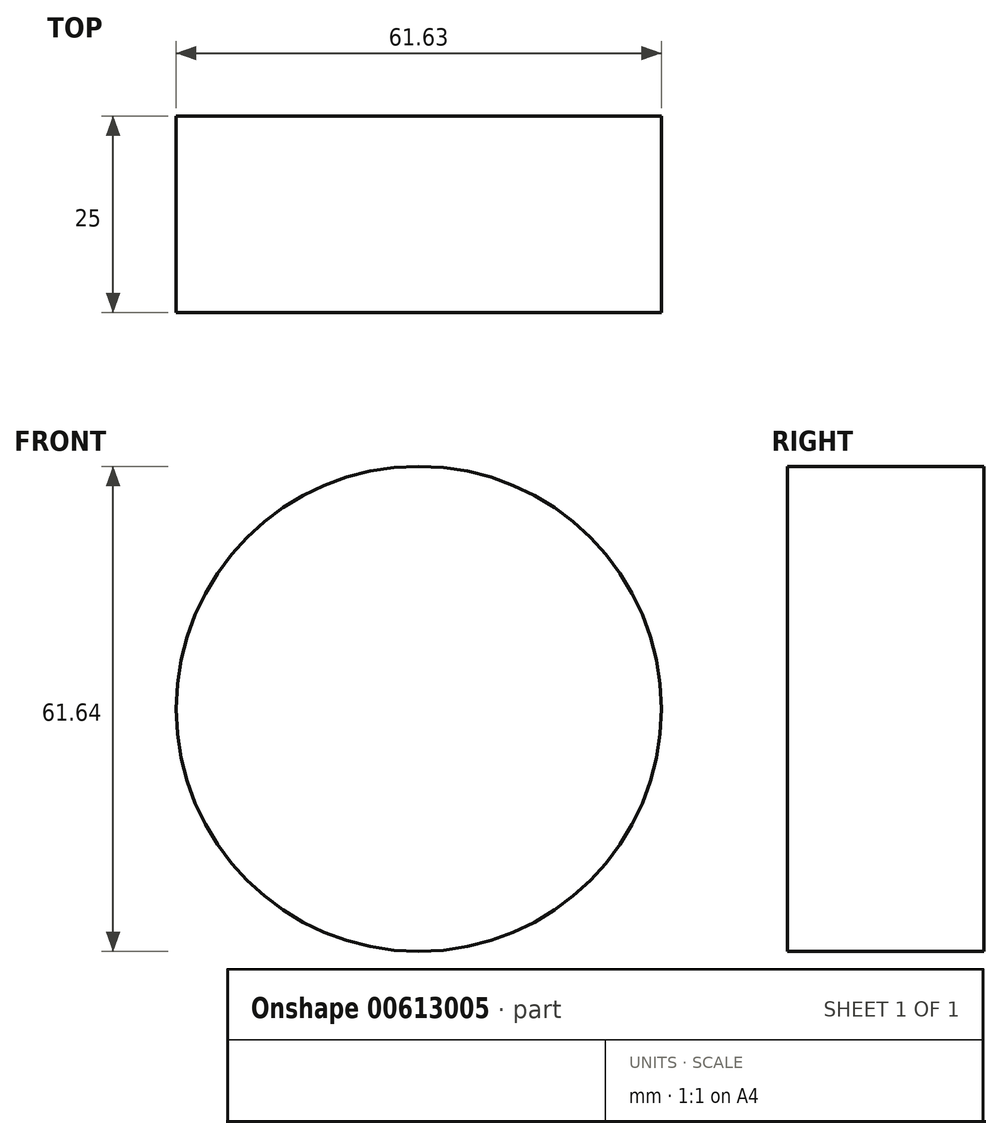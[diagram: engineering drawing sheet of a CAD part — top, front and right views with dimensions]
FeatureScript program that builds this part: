
annotation { "Feature Type Name" : "Feature", "Feature Type Description" : "" }
export const myFeature = defineFeature(function(context is Context, id is Id, definition is map)
    precondition{}
    {
        {
            var Q0;
            Q0=qCreatedBy(makeId("Front.planeOp"),FACE);
            var sketch = newSketch(context, id + "F0", { "sketchPlane" : qUnion([Q0])});
            skCircle(sketch, "E0", {"center": v(-25.1, -15.72) * mm, "radius": 30.82 * mm});
            skSolve(sketch);
        }
        {
            var Q0;
            Q0 = qSketchRegion(id + "F0", true);
            extrude(context, id + "F1", {"entities" : qUnion([Q0]), "depth" : 25 * mm, "offsetDistance" : 25 * mm});
        }
    });
